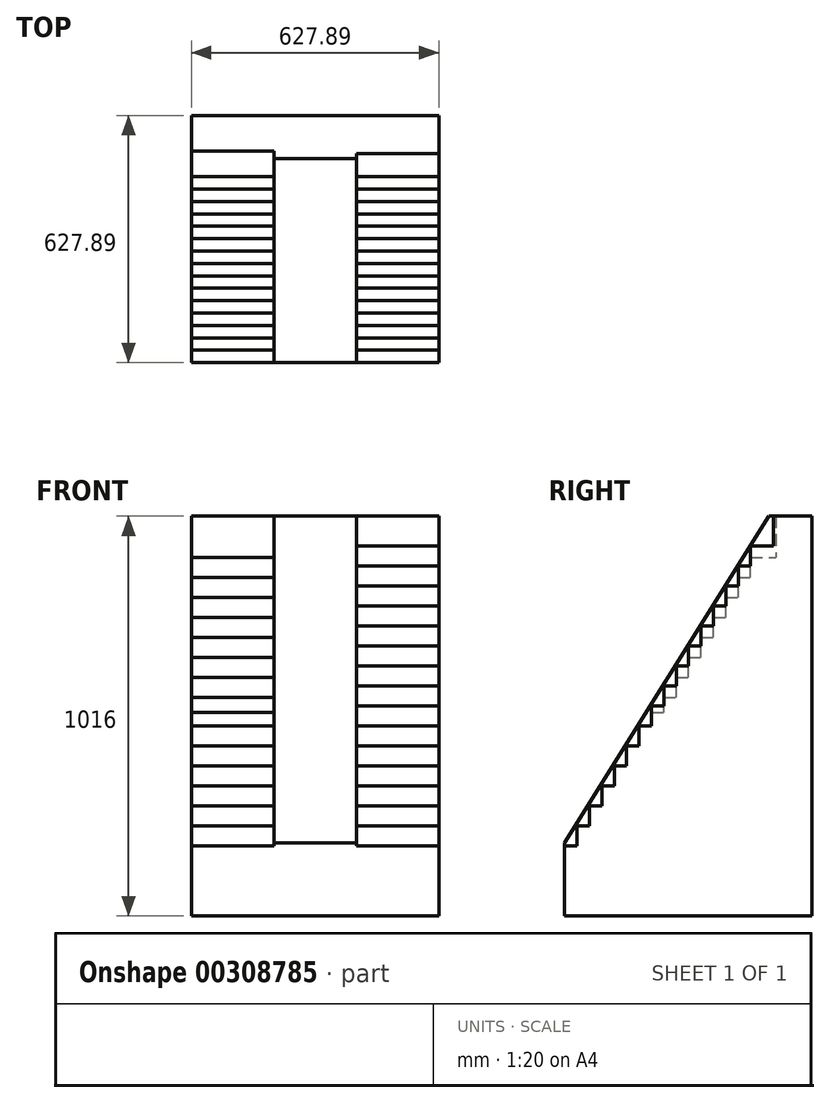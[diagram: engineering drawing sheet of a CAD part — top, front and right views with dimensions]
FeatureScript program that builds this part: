
annotation { "Feature Type Name" : "Feature", "Feature Type Description" : "" }
export const myFeature = defineFeature(function(context is Context, id is Id, definition is map)
    precondition{}
    {
        {
            var Q0;
            Q0=qCreatedBy(makeId("Top.planeOp"),FACE);
            var sketch = newSketch(context, id + "F0", { "sketchPlane" : qUnion([Q0])});
            skLineSegment(sketch, "E0.bottom", {"start": v(-161.52, 471.23) * mm, "end": v(466.37, 471.23) * mm});
            skLineSegment(sketch, "E0.top", {"start": v(-161.52, -156.66) * mm, "end": v(466.37, -156.66) * mm});
            skLineSegment(sketch, "E0.left", {"start": v(-161.52, 471.23) * mm, "end": v(-161.52, -156.66) * mm});
            skLineSegment(sketch, "E0.right", {"start": v(466.37, 471.23) * mm, "end": v(466.37, -156.66) * mm});
            skSolve(sketch);
        }
        {
            var Q0;
            Q0=makeQuery(id+"F0.imprint","IMPRINT",FACE,{"disambiguationData":[TD([[makeQuery(id+"F0.imprint","IMPRINT",EDGE,{"derivedFrom":sQuery(id+"F0.wireOp",EDGE,"E0.bottom")}),-1.0]])]});
            extrude(context, id + "F1", {"entities" : qUnion([Q0]), "depth" : 1016 * mm});
        }
        {
            var Q0;
            Q0=makeQuery(id+"F1.opExtrude","SWEPT_FACE",FACE,{"disambiguationData":[OSD([sQuery(id+"F0.wireOp",EDGE,"E0.right")])]});
            var sketch = newSketch(context, id + "F2", { "sketchPlane" : qUnion([Q0])});
            skLineSegment(sketch, "E1", {"start": v(-156.66, 177.8) * mm, "end": v(-125.16, 177.8) * mm});
            skLineSegment(sketch, "E2", {"start": v(-125.16, 177.8) * mm, "end": v(-125.16, 228.6) * mm});
            skLineSegment(sketch, "E3", {"start": v(-125.16, 228.6) * mm, "end": v(-93.67, 228.6) * mm});
            skLineSegment(sketch, "E4", {"start": v(-93.67, 228.6) * mm, "end": v(-93.67, 279.4) * mm});
            skLineSegment(sketch, "E5", {"start": v(-93.67, 279.4) * mm, "end": v(-62.17, 279.4) * mm});
            skLineSegment(sketch, "E6", {"start": v(-62.17, 279.4) * mm, "end": v(-62.17, 330.2) * mm});
            skLineSegment(sketch, "E7", {"start": v(-62.17, 330.2) * mm, "end": v(-30.68, 330.2) * mm});
            skLineSegment(sketch, "E8", {"start": v(-30.68, 330.2) * mm, "end": v(-30.68, 381) * mm});
            skLineSegment(sketch, "E9", {"start": v(-30.68, 381) * mm, "end": v(0.82, 381) * mm});
            skLineSegment(sketch, "E10", {"start": v(0.82, 381) * mm, "end": v(0.82, 431.8) * mm});
            skLineSegment(sketch, "E11", {"start": v(63.81, 482.6) * mm, "end": v(63.81, 533.4) * mm});
            skLineSegment(sketch, "E12", {"start": v(63.81, 533.4) * mm, "end": v(95.3, 533.4) * mm});
            skLineSegment(sketch, "E13", {"start": v(95.3, 533.4) * mm, "end": v(95.3, 584.2) * mm});
            skLineSegment(sketch, "E14", {"start": v(95.3, 584.2) * mm, "end": v(126.8, 584.2) * mm});
            skLineSegment(sketch, "E15", {"start": v(126.8, 584.2) * mm, "end": v(126.8, 635) * mm});
            skLineSegment(sketch, "E16", {"start": v(126.8, 635) * mm, "end": v(158.3, 635) * mm});
            skLineSegment(sketch, "E17", {"start": v(158.3, 635) * mm, "end": v(158.3, 685.8) * mm});
            skLineSegment(sketch, "E18", {"start": v(158.3, 685.8) * mm, "end": v(189.8, 685.8) * mm});
            skLineSegment(sketch, "E19", {"start": v(189.8, 685.8) * mm, "end": v(189.8, 736.6) * mm});
            skLineSegment(sketch, "E20", {"start": v(189.8, 736.6) * mm, "end": v(221.3, 736.6) * mm});
            skLineSegment(sketch, "E21", {"start": v(221.3, 736.6) * mm, "end": v(221.3, 787.4) * mm});
            skLineSegment(sketch, "E22", {"start": v(221.3, 787.4) * mm, "end": v(252.79, 787.4) * mm});
            skLineSegment(sketch, "E23", {"start": v(252.79, 787.4) * mm, "end": v(252.79, 838.2) * mm});
            skLineSegment(sketch, "E24", {"start": v(252.79, 838.2) * mm, "end": v(284.28, 838.2) * mm});
            skLineSegment(sketch, "E25", {"start": v(284.28, 838.2) * mm, "end": v(284.28, 889) * mm});
            skLineSegment(sketch, "E26", {"start": v(284.28, 889) * mm, "end": v(315.78, 889) * mm});
            skLineSegment(sketch, "E27", {"start": v(315.78, 889) * mm, "end": v(315.78, 939.8) * mm});
            skLineSegment(sketch, "E28", {"start": v(0.82, 431.8) * mm, "end": v(32.32, 431.8) * mm});
            skLineSegment(sketch, "E29", {"start": v(32.32, 431.8) * mm, "end": v(32.32, 482.6) * mm});
            skLineSegment(sketch, "E30", {"start": v(32.32, 482.6) * mm, "end": v(63.81, 482.6) * mm});
            skLineSegment(sketch, "E31", {"start": v(-156.66, 177.8) * mm, "end": v(-156.66, 1016) * mm});
            skLineSegment(sketch, "E32", {"start": v(-156.66, 1016) * mm, "end": v(373.9, 1016) * mm});
            skLineSegment(sketch, "E33", {"start": v(315.78, 939.8) * mm, "end": v(374.18, 939.8) * mm});
            skLineSegment(sketch, "E34", {"start": v(374.18, 939.8) * mm, "end": v(373.9, 1016) * mm});
            skSolve(sketch);
        }
        {
            var Q0;
            Q0=makeQuery(id+"F2.imprint","IMPRINT",FACE,{"disambiguationData":[TD([[makeQuery(id+"F2.imprint","IMPRINT",EDGE,{"derivedFrom":sQuery(id+"F2.wireOp",EDGE,"E1")}),1.0]])]});
            extrude(context, id + "F3", {"entities" : qUnion([Q0]), "operationType" : NewBodyOperationType.REMOVE, "oppositeDirection" : true, "depth" : 209.3 * mm});
        }
        {
            var Q0;
            Q0=makeQuery(id+"F3.boolean.opBoolean","COPY",FACE,{"derivedFrom":makeQuery(id+"F3.opExtrude","CAP_FACE",FACE,{"disambiguationData":[OSD([sQuery(id+"F2.wireOp",EDGE,"E1"),sQuery(id+"F2.wireOp",EDGE,"E2"),sQuery(id+"F2.wireOp",EDGE,"E3"),sQuery(id+"F2.wireOp",EDGE,"E4"),sQuery(id+"F2.wireOp",EDGE,"E5"),sQuery(id+"F2.wireOp",EDGE,"E6"),sQuery(id+"F2.wireOp",EDGE,"E7"),sQuery(id+"F2.wireOp",EDGE,"E8"),sQuery(id+"F2.wireOp",EDGE,"E9"),sQuery(id+"F2.wireOp",EDGE,"E10"),sQuery(id+"F2.wireOp",EDGE,"E11"),sQuery(id+"F2.wireOp",EDGE,"E12"),sQuery(id+"F2.wireOp",EDGE,"E13"),sQuery(id+"F2.wireOp",EDGE,"E14"),sQuery(id+"F2.wireOp",EDGE,"E15"),sQuery(id+"F2.wireOp",EDGE,"E16"),sQuery(id+"F2.wireOp",EDGE,"E17"),sQuery(id+"F2.wireOp",EDGE,"E18"),sQuery(id+"F2.wireOp",EDGE,"E19"),sQuery(id+"F2.wireOp",EDGE,"E20"),sQuery(id+"F2.wireOp",EDGE,"E21"),sQuery(id+"F2.wireOp",EDGE,"E22"),sQuery(id+"F2.wireOp",EDGE,"E23"),sQuery(id+"F2.wireOp",EDGE,"E24"),sQuery(id+"F2.wireOp",EDGE,"E25"),sQuery(id+"F2.wireOp",EDGE,"E26"),sQuery(id+"F2.wireOp",EDGE,"E27"),sQuery(id+"F2.wireOp",EDGE,"E28"),sQuery(id+"F2.wireOp",EDGE,"E29"),sQuery(id+"F2.wireOp",EDGE,"E30"),sQuery(id+"F2.wireOp",EDGE,"E31"),sQuery(id+"F2.wireOp",EDGE,"E32"),sQuery(id+"F2.wireOp",EDGE,"st6rdCQ2-XGsa-vdC0-6qYG-qleKJLN3XYLF"),sQuery(id+"F2.wireOp",EDGE,"ESZmzlLe-aRCl-FKnC-ftiQ-nmJHwnA4npTW")])],"isStart":false})});
            var sketch = newSketch(context, id + "F4", { "sketchPlane" : qUnion([Q0])});
            skLineSegment(sketch, "E35", {"start": v(361.93, 1016) * mm, "end": v(-156.66, 1016) * mm});
            skLineSegment(sketch, "E36", {"start": v(-156.66, 1016) * mm, "end": v(-156.66, 185.63) * mm});
            skLineSegment(sketch, "E37", {"start": v(-156.66, 185.63) * mm, "end": v(361.93, 1016) * mm});
            skSolve(sketch);
        }
        {
            var Q0;
            Q0=makeQuery(id+"F4.imprint","IMPRINT",FACE,{"disambiguationData":[TD([[makeQuery(id+"F4.imprint","IMPRINT",EDGE,{"derivedFrom":sQuery(id+"F4.wireOp",EDGE,"E35")}),1.0]])]});
            extrude(context, id + "F5", {"entities" : qUnion([Q0]), "operationType" : NewBodyOperationType.REMOVE, "oppositeDirection" : true, "depth" : 209.3 * mm});
        }
        {
            var Q0;
            Q0=makeQuery(id+"F1.opExtrude","SWEPT_FACE",FACE,{"disambiguationData":[OSD([sQuery(id+"F0.wireOp",EDGE,"E0.left")])]});
            var sketch = newSketch(context, id + "F6", { "sketchPlane" : qUnion([Q0])});
            skLineSegment(sketch, "E38", {"start": v(-380.54, 1016) * mm, "end": v(-380.54, 911.2) * mm});
            skLineSegment(sketch, "E39.MirrorCS", {"start": v(-126.8, 606.4) * mm, "end": v(-158.29, 606.4) * mm});
            skLineSegment(sketch, "E40.MirrorCS", {"start": v(-32.3, 431.8) * mm, "end": v(-32.3, 482.6) * mm});
            skLineSegment(sketch, "E41.MirrorCS", {"start": v(-158.29, 657.2) * mm, "end": v(-189.78, 657.2) * mm});
            skLineSegment(sketch, "E42.MirrorCS", {"start": v(-315.77, 860.4) * mm, "end": v(-315.77, 911.2) * mm});
            skLineSegment(sketch, "E43.MirrorCS", {"start": v(-284.27, 860.4) * mm, "end": v(-315.77, 860.4) * mm});
            skLineSegment(sketch, "E44.MirrorCS", {"start": v(-284.27, 809.6) * mm, "end": v(-284.27, 860.4) * mm});
            skLineSegment(sketch, "E45.MirrorCS", {"start": v(-32.3, 482.6) * mm, "end": v(-63.8, 482.61) * mm});
            skLineSegment(sketch, "E46.MirrorCS", {"start": v(-252.78, 809.6) * mm, "end": v(-284.27, 809.6) * mm});
            skLineSegment(sketch, "E47.MirrorCS", {"start": v(-0.8, 431.8) * mm, "end": v(-32.3, 431.8) * mm});
            skLineSegment(sketch, "E48.MirrorCS", {"start": v(-63.8, 482.61) * mm, "end": v(-63.8, 517.45) * mm});
            skLineSegment(sketch, "E49.MirrorCS", {"start": v(-158.29, 606.4) * mm, "end": v(-158.29, 657.2) * mm});
            skLineSegment(sketch, "E50.MirrorCS", {"start": v(-189.78, 657.2) * mm, "end": v(-189.78, 708) * mm});
            skLineSegment(sketch, "E51.MirrorCS", {"start": v(-221.28, 758.8) * mm, "end": v(-252.78, 758.8) * mm});
            skLineSegment(sketch, "E52.MirrorCS", {"start": v(-0.8, 381) * mm, "end": v(-0.8, 431.8) * mm});
            skLineSegment(sketch, "E53.MirrorCS", {"start": v(-315.77, 911.2) * mm, "end": v(-380.54, 911.2) * mm});
            skLineSegment(sketch, "E54.MirrorCS", {"start": v(-252.78, 758.8) * mm, "end": v(-252.78, 809.6) * mm});
            skLineSegment(sketch, "E55.MirrorCS", {"start": v(156.67, 177.8) * mm, "end": v(125.18, 177.8) * mm});
            skLineSegment(sketch, "E56.MirrorCS", {"start": v(30.69, 381) * mm, "end": v(-0.8, 381) * mm});
            skLineSegment(sketch, "E57.MirrorCS", {"start": v(30.69, 330.2) * mm, "end": v(30.69, 381) * mm});
            skLineSegment(sketch, "E58.MirrorCS", {"start": v(-221.28, 708) * mm, "end": v(-221.28, 758.8) * mm});
            skLineSegment(sketch, "E59.MirrorCS", {"start": v(-126.8, 555.6) * mm, "end": v(-126.8, 606.4) * mm});
            skLineSegment(sketch, "E60.MirrorCS", {"start": v(62.18, 279.4) * mm, "end": v(62.18, 330.2) * mm});
            skLineSegment(sketch, "E61.MirrorCS", {"start": v(62.18, 330.2) * mm, "end": v(30.69, 330.2) * mm});
            skLineSegment(sketch, "E62.MirrorCS", {"start": v(93.68, 279.4) * mm, "end": v(62.18, 279.4) * mm});
            skLineSegment(sketch, "E63.MirrorCS", {"start": v(125.18, 177.8) * mm, "end": v(125.18, 228.6) * mm});
            skLineSegment(sketch, "E64.MirrorCS", {"start": v(125.18, 228.6) * mm, "end": v(93.68, 228.6) * mm});
            skLineSegment(sketch, "E65.MirrorCS", {"start": v(-95.3, 517.45) * mm, "end": v(-95.3, 555.6) * mm});
            skLineSegment(sketch, "E66.MirrorCS", {"start": v(-95.3, 555.6) * mm, "end": v(-126.8, 555.6) * mm});
            skLineSegment(sketch, "E67.MirrorCS", {"start": v(-63.8, 517.45) * mm, "end": v(-95.3, 517.45) * mm});
            skLineSegment(sketch, "E68.MirrorCS", {"start": v(93.68, 228.6) * mm, "end": v(93.68, 279.4) * mm});
            skLineSegment(sketch, "E69.MirrorCS", {"start": v(-189.78, 708) * mm, "end": v(-221.28, 708) * mm});
            skLineSegment(sketch, "E70.MirrorCS", {"start": v(156.67, 1016) * mm, "end": v(-380.54, 1016) * mm});
            skLineSegment(sketch, "E71.MirrorCS", {"start": v(156.67, 177.8) * mm, "end": v(156.67, 1016) * mm});
            skSolve(sketch);
        }
        {
            var Q0;
            Q0=makeQuery(id+"F6.imprint","IMPRINT",FACE,{"disambiguationData":[TD([[makeQuery(id+"F6.imprint","IMPRINT",EDGE,{"derivedFrom":sQuery(id+"F6.wireOp",EDGE,"E39.MirrorCS")}),-1.0]])]});
            extrude(context, id + "F7", {"entities" : qUnion([Q0]), "operationType" : NewBodyOperationType.REMOVE, "oppositeDirection" : true, "depth" : 209.3 * mm});
        }
    });
